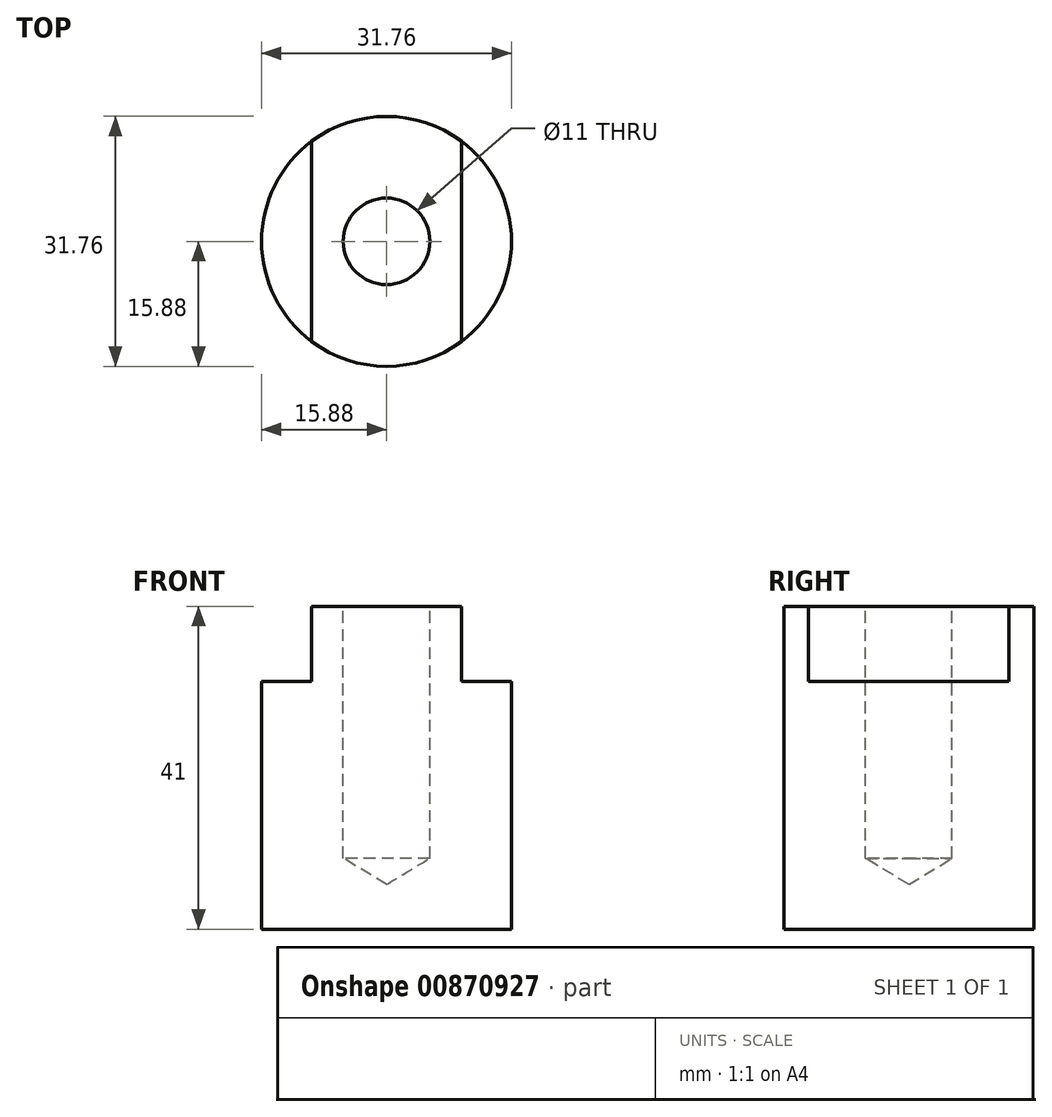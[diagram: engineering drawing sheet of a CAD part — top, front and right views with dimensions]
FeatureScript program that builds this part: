
annotation { "Feature Type Name" : "Feature", "Feature Type Description" : "" }
export const myFeature = defineFeature(function(context is Context, id is Id, definition is map)
    precondition{}
    {
        {
            var Q0;
            Q0=qCreatedBy(makeId("Top.planeOp"),FACE);
            var sketch = newSketch(context, id + "F0", { "sketchPlane" : qUnion([Q0])});
            skCircle(sketch, "E0", {"center": v(0, 0) * mm, "radius": 15.88 * mm});
            skSolve(sketch);
        }
        {
            var Q0;
            Q0 = qSketchRegion(id + "F0", true);
            extrude(context, id + "F1", {"entities" : qUnion([Q0]), "depth" : 41 * mm, "offsetDistance" : 25.4 * mm});
        }
        {
            var Q0;
            Q0=qCreatedBy(makeId("Front.planeOp"),FACE);
            var sketch = newSketch(context, id + "F2", { "sketchPlane" : qUnion([Q0])});
            skLineSegment(sketch, "E1.bottom", {"start": v(-16.5, 41) * mm, "end": v(-9.5, 41) * mm});
            skLineSegment(sketch, "E1.top", {"start": v(-16.5, 31.5) * mm, "end": v(-9.5, 31.5) * mm});
            skLineSegment(sketch, "E1.left", {"start": v(-16.5, 41) * mm, "end": v(-16.5, 31.5) * mm});
            skLineSegment(sketch, "E1.right", {"start": v(-9.5, 41) * mm, "end": v(-9.5, 31.5) * mm});
            skLineSegment(sketch, "E2.bottom", {"start": v(9.5, 41) * mm, "end": v(16.5, 41) * mm});
            skLineSegment(sketch, "E2.top", {"start": v(9.5, 31.5) * mm, "end": v(16.5, 31.5) * mm});
            skLineSegment(sketch, "E2.left", {"start": v(9.5, 41) * mm, "end": v(9.5, 31.5) * mm});
            skLineSegment(sketch, "E2.right", {"start": v(16.5, 41) * mm, "end": v(16.5, 31.5) * mm});
            skSolve(sketch);
        }
        {
            var Q0;
            Q0 = qSketchRegion(id + "F2", true);
            extrude(context, id + "F3", {"entities" : qUnion([Q0]), "operationType" : NewBodyOperationType.REMOVE, "endBound" : BoundingType.SYMMETRIC, "oppositeDirection" : true, "depth" : 50 * mm, "offsetDistance" : 25 * mm});
        }
        {
            var Q0;
            Q0=makeQuery(id+"F1.opExtrude","CAP_FACE",FACE,{"disambiguationData":[OSD([sQuery(id+"F0.wireOp",EDGE,"E0")])],"isStart":false});
            var sketch = newSketch(context, id + "F4", { "sketchPlane" : qUnion([Q0])});
            skPoint(sketch, "E3", {"position": v(0, 0) * mm});
            skSolve(sketch);
        }
        {
            var Q0;
            Q0=sQuery(id+"F4.wireOp",VERTEX,"E3");
            var Q1;
            Q1=makeQuery(id+"F1.opExtrude","SWEPT_BODY",BODY,{"disambiguationData":[OSD([sQuery(id+"F0.wireOp",EDGE,"E0")])]});
            hole(context, id + "F5", {"style" : HoleStyle.SIMPLE, "endStyle" : HoleEndStyle.BLIND, "standardTappedOrClearance" : lookupTablePath({ "fit" : "Normal", "standard" : "ISO", "size" : "M10", "type" : "Clearance" }), "standardBlindInLast" : lookupTablePath({ "fit" : "Standard", "standard" : "ISO", "size" : "M10", "type" : "Clearance" }), "holeDiameter" : 11 * mm, "majorDiameter" : 10 * mm, "holeDepth" : 32 * mm, "isTappedThrough" : true, "tappedDepth" : 27.9 * mm, "tapClearance" : 3, "startFromSketch" : true, "locations" : qUnion([Q0]), "scope" : qUnion([Q1])});
        }
    });
